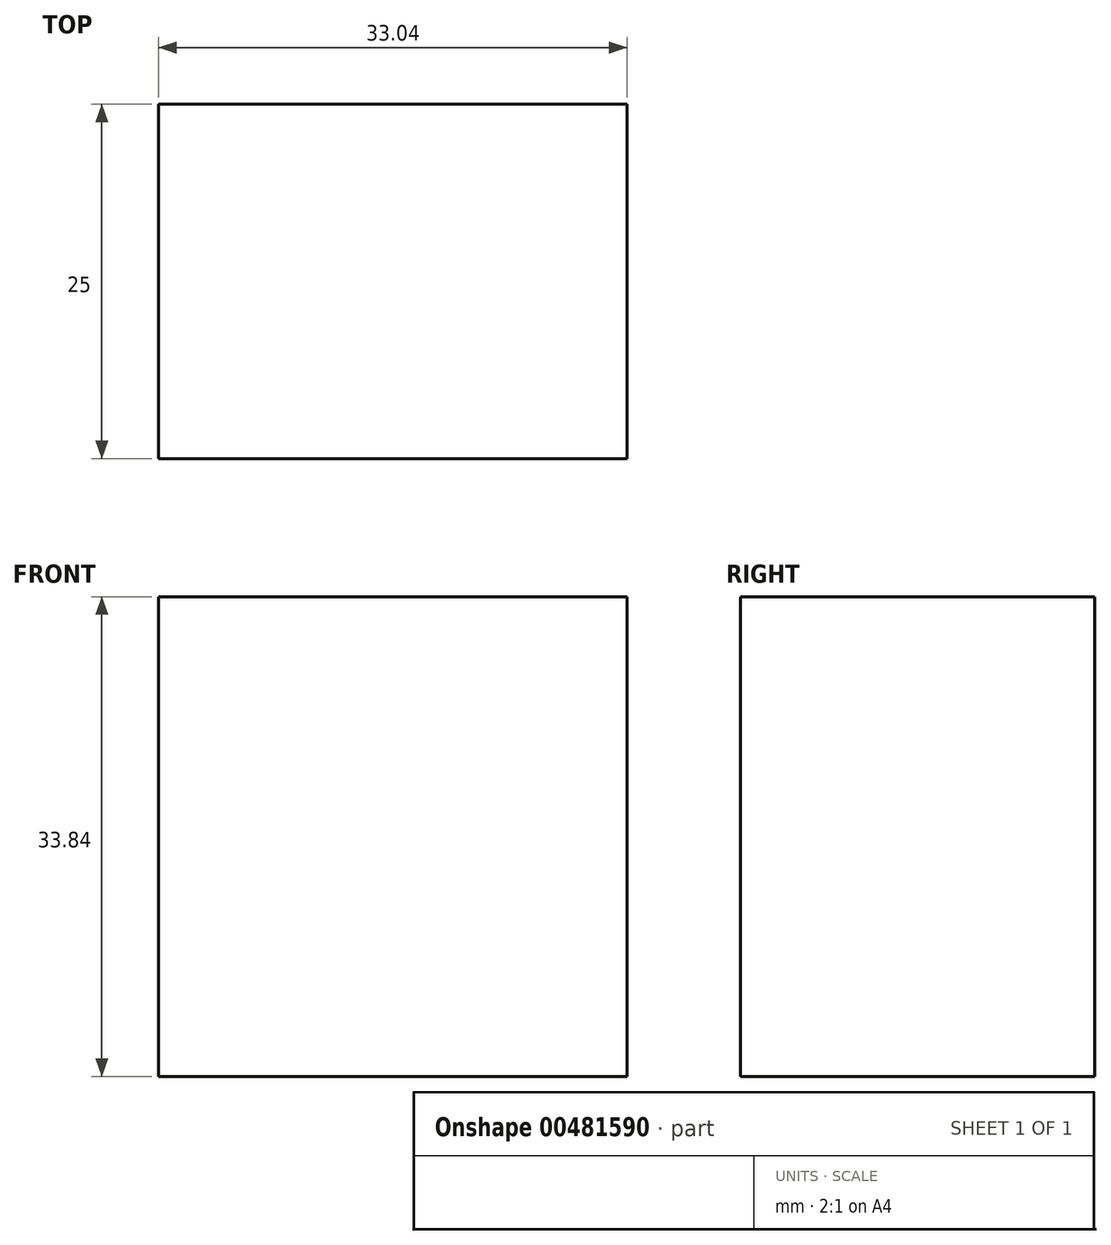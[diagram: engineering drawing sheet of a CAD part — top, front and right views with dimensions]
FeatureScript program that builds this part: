
annotation { "Feature Type Name" : "Feature", "Feature Type Description" : "" }
export const myFeature = defineFeature(function(context is Context, id is Id, definition is map)
    precondition{}
    {
        {
            var Q0;
            Q0=qCreatedBy(makeId("Front.planeOp"),FACE);
            var sketch = newSketch(context, id + "F0", { "sketchPlane" : qUnion([Q0])});
            skLineSegment(sketch, "E0.bottom", {"start": v(0, 0) * mm, "end": v(-33.04, 0) * mm});
            skLineSegment(sketch, "E0.top", {"start": v(0, 33.84) * mm, "end": v(-33.04, 33.84) * mm});
            skLineSegment(sketch, "E0.left", {"start": v(0, 0) * mm, "end": v(0, 33.84) * mm});
            skLineSegment(sketch, "E0.right", {"start": v(-33.04, 0) * mm, "end": v(-33.04, 33.84) * mm});
            skSolve(sketch);
        }
        {
            var Q0;
            Q0 = qSketchRegion(id + "F0", true);
            extrude(context, id + "F1", {"entities" : qUnion([Q0]), "depth" : 25 * mm});
        }
    });
